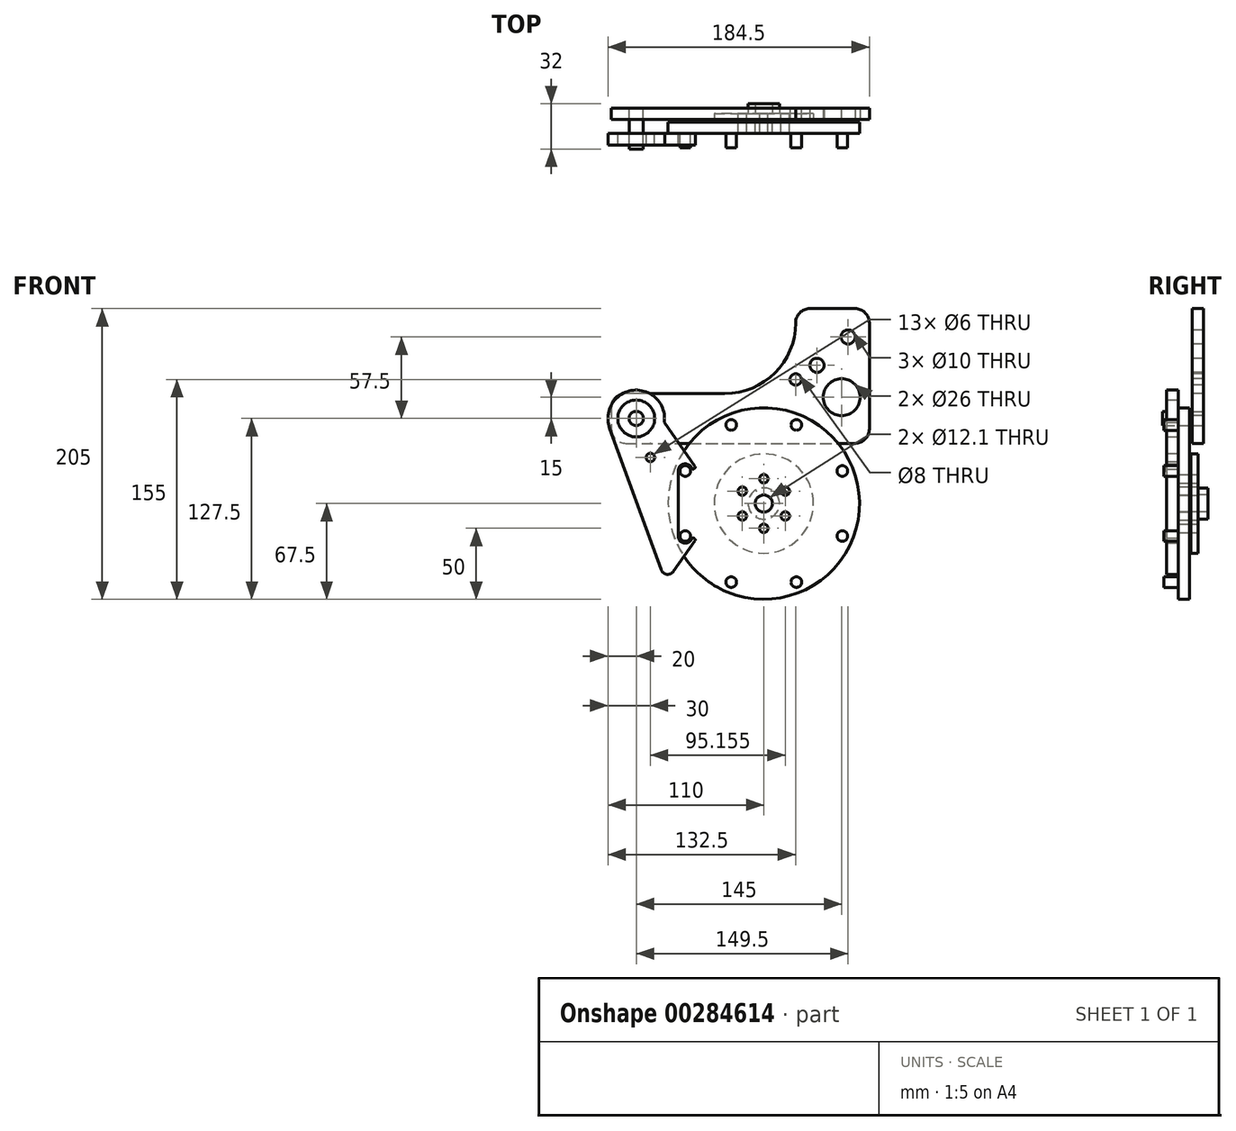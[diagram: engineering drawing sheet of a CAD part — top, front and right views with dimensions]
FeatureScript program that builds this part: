
annotation { "Feature Type Name" : "Feature", "Feature Type Description" : "" }
export const myFeature = defineFeature(function(context is Context, id is Id, definition is map)
    precondition{}
    {
        {
            var Q0;
            Q0=qCreatedBy(makeId("Front.planeOp"),FACE);
            var sketch = newSketch(context, id + "F0", { "sketchPlane" : qUnion([Q0])});
            skCircle(sketch, "E0", {"center": v(0, 0) * mm, "radius": 67.5 * mm});
            skCircle(sketch, "E1", {"center": v(0, 0) * mm, "radius": 6.05 * mm});
            skSolve(sketch);
        }
        {
            var Q0;
            Q0=qSketchRegion(id+"F0",true);
            extrude(context, id + "F1", {"entities" : qUnion([Q0]), "depth" : 5 * mm, "hasSecondDirection" : true, "secondDirectionOppositeDirection" : true, "secondDirectionDepth" : 3 * mm});
        }
        {
            var Q0;
            Q0=makeQuery(id+"F1.opExtrude","CAP_FACE",FACE,{"disambiguationData":[OSD([sQuery(id+"F0.wireOp",EDGE,"E0"),sQuery(id+"F0.wireOp",EDGE,"E1")])],"isStart":false});
            var sketch = newSketch(context, id + "F2", { "sketchPlane" : qUnion([Q0])});
            skCircle(sketch, "E2", {"center": v(0, 0) * mm, "radius": 60 * mm, "construction": true});
            skCircle(sketch, "E3", {"center": v(0, 60) * mm, "radius": 3.75 * mm});
            skCircle(sketch, "E4.1.0", {"center": v(-42.43, 42.43) * mm, "radius": 3.75 * mm});
            skCircle(sketch, "E4.2.0", {"center": v(-60, 0) * mm, "radius": 3.75 * mm});
            skCircle(sketch, "E4.3.0", {"center": v(-42.43, -42.43) * mm, "radius": 3.75 * mm});
            skCircle(sketch, "E4.4.0", {"center": v(0, -60) * mm, "radius": 3.75 * mm});
            skCircle(sketch, "E4.5.0", {"center": v(42.43, -42.43) * mm, "radius": 3.75 * mm});
            skCircle(sketch, "E4.6.0", {"center": v(60, 0) * mm, "radius": 3.75 * mm});
            skCircle(sketch, "E4.7.0", {"center": v(42.43, 42.43) * mm, "radius": 3.75 * mm});
            skPoint(sketch, "E5", {"position": v(0, -77) * mm});
            skSolve(sketch);
        }
        {
            var Q0;
            Q0=qSketchRegion(id+"F2",true);
            extrude(context, id + "F3", {"entities" : qUnion([Q0]), "operationType" : NewBodyOperationType.ADD, "depth" : 10 * mm});
        }
        {
            var Q0;
            Q0=qCreatedBy(makeId("Right.planeOp"),FACE);
            var sketch = newSketch(context, id + "F4", { "sketchPlane" : qUnion([Q0])});
            skLineSegment(sketch, "E6", {"start": v(-64.67, -77) * mm, "end": v(70.6, -77) * mm});
            skLineSegment(sketch, "E7", {"start": v(-72, 0) * mm, "end": v(117.3, 0) * mm});
            skLineSegment(sketch, "E8", {"start": v(-81.45, 67) * mm, "end": v(84.45, 67) * mm});
            skSolve(sketch);
        }
        {
            var Q0;
            Q0=makeQuery(id+"F1.opExtrude","CAP_FACE",FACE,{"disambiguationData":[OSD([sQuery(id+"F0.wireOp",EDGE,"E0"),sQuery(id+"F0.wireOp",EDGE,"E1")])],"isStart":false});
            var sketch = newSketch(context, id + "F5", { "sketchPlane" : qUnion([Q0])});
            skLineSegment(sketch, "E9", {"start": v(22.5, 127.5) * mm, "end": v(22.5, 127.5) * mm});
            skLineSegment(sketch, "E10", {"start": v(-27.5, 77.5) * mm, "end": v(-97.5, 77.5) * mm});
            skLineSegment(sketch, "E11", {"start": v(-107.5, 67.5) * mm, "end": v(-107.5, 52.5) * mm});
            skLineSegment(sketch, "E12", {"start": v(-97.5, 42.5) * mm, "end": v(-75.62, 42.5) * mm});
            skLineSegment(sketch, "E13", {"start": v(64.5, 137.5) * mm, "end": v(32.5, 137.5) * mm});
            skCircle(sketch, "E14", {"center": v(55, 75) * mm, "radius": 13 * mm});
            skCircle(sketch, "E15", {"center": v(-90, 60) * mm, "radius": 5 * mm});
            skCircle(sketch, "E16", {"center": v(59.5, 117.5) * mm, "radius": 5 * mm});
            skCircle(sketch, "E17", {"center": v(37.5, 97.5) * mm, "radius": 5 * mm});
            skPoint(sketch, "E18.visualSharp", {"position": v(-107.5, 77.5) * mm});
            skArc(sketch, "E18.filletArc", {"start": v(-97.5, 77.5) * mm, "mid": v(-104.57, 74.57) * mm, "end": v(-107.5, 67.5) * mm});
            skPoint(sketch, "E19.visualSharp", {"position": v(-107.5, 42.5) * mm});
            skArc(sketch, "E19.filletArc", {"start": v(-107.5, 52.5) * mm, "mid": v(-104.57, 45.43) * mm, "end": v(-97.5, 42.5) * mm});
            skArc(sketch, "E20.filletArc", {"start": v(-27.5, 77.5) * mm, "mid": v(7.86, 92.14) * mm, "end": v(22.5, 127.5) * mm});
            skArc(sketch, "E21.filletArc", {"start": v(32.5, 137.5) * mm, "mid": v(25.43, 134.57) * mm, "end": v(22.5, 127.5) * mm});
            skLineSegment(sketch, "E22", {"start": v(74.5, 127.5) * mm, "end": v(74.5, 52.5) * mm});
            skPoint(sketch, "E23.visualSharp", {"position": v(74.5, 137.5) * mm});
            skArc(sketch, "E23.filletArc", {"start": v(74.5, 127.5) * mm, "mid": v(71.57, 134.57) * mm, "end": v(64.5, 137.5) * mm});
            skPoint(sketch, "E24.visualSharp", {"position": v(74.5, 42.5) * mm});
            skArc(sketch, "E24.filletArc", {"start": v(64.5, 42.5) * mm, "mid": v(71.57, 45.43) * mm, "end": v(74.5, 52.5) * mm});
            skLineSegment(sketch, "E25.trimOffspring", {"start": v(-75.62, 42.5) * mm, "end": v(64.5, 42.5) * mm});
            skCircle(sketch, "E26", {"center": v(22.5, 87.5) * mm, "radius": 4 * mm});
            skSolve(sketch);
        }
        {
            var Q0;
            Q0=makeQuery(id+"F1.opExtrude","SWEPT_BODY",BODY,{"disambiguationData":[OSD([sQuery(id+"F0.wireOp",EDGE,"E0"),sQuery(id+"F0.wireOp",EDGE,"E1")])]});
            var Q1;
            Q1=sQuery(id+"F4.wireOp",EDGE,"E7");
            transform(context, id + "F6", {"entities" : qUnion([Q0]), "transformType" : TransformType.ROTATION, "transformAxis" : qUnion([Q1]), "angle" : 22.5 * degree, "makeCopy" : false});
        }
        {
            var Q0;
            Q0=qSketchRegion(id+"F5",true);
            extrude(context, id + "F7", {"entities" : qUnion([Q0]), "oppositeDirection" : true, "depth" : 8 * mm});
        }
        {
            var Q0;
            Q0=makeQuery(id+"F7.opExtrude","SWEPT_BODY",BODY,{"disambiguationData":[OSD([sQuery(id+"F5.wireOp",EDGE,"E9"),sQuery(id+"F5.wireOp",EDGE,"E10"),sQuery(id+"F5.wireOp",EDGE,"E11"),sQuery(id+"F5.wireOp",EDGE,"E12"),sQuery(id+"F5.wireOp",EDGE,"E13"),sQuery(id+"F5.wireOp",EDGE,"E14"),sQuery(id+"F5.wireOp",EDGE,"E15"),sQuery(id+"F5.wireOp",EDGE,"E16"),sQuery(id+"F5.wireOp",EDGE,"E17"),sQuery(id+"F5.wireOp",EDGE,"E18.filletArc"),sQuery(id+"F5.wireOp",EDGE,"E19.filletArc"),sQuery(id+"F5.wireOp",EDGE,"E20.filletArc"),sQuery(id+"F5.wireOp",EDGE,"E21.filletArc"),sQuery(id+"F5.wireOp",EDGE,"E22"),sQuery(id+"F5.wireOp",EDGE,"E23.filletArc"),sQuery(id+"F5.wireOp",EDGE,"E24.filletArc"),sQuery(id+"F5.wireOp",EDGE,"E25.trimOffspring")])]});
            transform(context, id + "F8", {"entities" : qUnion([Q0]), "transformType" : TransformType.TRANSLATION_3D, "dx" : 0 * mm, "dy" : 10 * mm, "dz" : 0 * mm, "makeCopy" : false});
        }
        {
            var Q0;
            Q0=makeQuery(id+"F1.opExtrude","CAP_FACE",FACE,{"disambiguationData":[OSD([sQuery(id+"F0.wireOp",EDGE,"E0"),sQuery(id+"F0.wireOp",EDGE,"E1")])],"isStart":false});
            var sketch = newSketch(context, id + "F9", { "sketchPlane" : qUnion([Q0])});
            skCircle(sketch, "E27", {"center": v(-90, 60) * mm, "radius": 13 * mm});
            skArc(sketch, "E28", {"start": v(-70.2, 57.14) * mm, "mid": v(-92.05, 79.9) * mm, "end": v(-108.8, 53.16) * mm});
            skLineSegment(sketch, "E29", {"start": v(-48.55, -26.21) * mm, "end": v(-63.67, -47.8) * mm});
            skLineSegment(sketch, "E30", {"start": v(-72.47, -46.65) * mm, "end": v(-108.8, 53.16) * mm});
            skPoint(sketch, "E31.visualSharp", {"position": v(-69.18, -55.67) * mm});
            skArc(sketch, "E31.filletArc", {"start": v(-72.47, -46.65) * mm, "mid": v(-68.42, -49.9) * mm, "end": v(-63.67, -47.8) * mm});
            skCircle(sketch, "E32", {"center": v(-80, 32.5) * mm, "radius": 3 * mm});
            skArc(sketch, "E33", {"start": v(-60.43, -22.96) * mm, "mid": v(-56.44, -27.86) * mm, "end": v(-50.84, -24.93) * mm});
            skLineSegment(sketch, "E34", {"start": v(-48.87, -24.77) * mm, "end": v(-49.42, -24.46) * mm});
            skPoint(sketch, "E35.visualSharp", {"position": v(-47.93, -25.32) * mm});
            skArc(sketch, "E35.filletArc", {"start": v(-48.55, -26.21) * mm, "mid": v(-48.4, -25.42) * mm, "end": v(-48.87, -24.77) * mm});
            skArc(sketch, "E36", {"start": v(-50.84, 24.93) * mm, "mid": v(-56.44, 27.86) * mm, "end": v(-60.43, 22.96) * mm});
            skLineSegment(sketch, "E37", {"start": v(-60.43, 22.96) * mm, "end": v(-60.43, -22.96) * mm});
            skLineSegment(sketch, "E38", {"start": v(-70.2, 57.14) * mm, "end": v(-48.55, 26.21) * mm});
            skLineSegment(sketch, "E39", {"start": v(-55.43, -22.96) * mm, "end": v(-50.5, -23.83) * mm, "construction": true});
            skPoint(sketch, "E40.visualSharp", {"position": v(-50.5, -23.83) * mm});
            skArc(sketch, "E40.filletArc", {"start": v(-49.42, -24.46) * mm, "mid": v(-50.23, -24.38) * mm, "end": v(-50.84, -24.93) * mm});
            skLineSegment(sketch, "E41", {"start": v(-55.43, 22.96) * mm, "end": v(-50.5, 23.83) * mm, "construction": true});
            skLineSegment(sketch, "E42", {"start": v(-48.87, 24.77) * mm, "end": v(-49.42, 24.46) * mm});
            skPoint(sketch, "E43.visualSharp", {"position": v(-50.5, 23.83) * mm});
            skArc(sketch, "E43.filletArc", {"start": v(-50.84, 24.93) * mm, "mid": v(-50.23, 24.38) * mm, "end": v(-49.42, 24.46) * mm});
            skPoint(sketch, "E44.visualSharp", {"position": v(-47.93, 25.32) * mm});
            skArc(sketch, "E44.filletArc", {"start": v(-48.87, 24.77) * mm, "mid": v(-48.4, 25.42) * mm, "end": v(-48.55, 26.21) * mm});
            skSolve(sketch);
        }
        {
            var Q0;
            Q0=qSketchRegion(id+"F9",true);
            extrude(context, id + "F10", {"entities" : qUnion([Q0]), "depth" : 8 * mm});
        }
        {
            var Q0;
            Q0=qCreatedBy(makeId("Top.planeOp"),FACE);
            var sketch = newSketch(context, id + "F11", { "sketchPlane" : qUnion([Q0])});
            skLineSegment(sketch, "E45", {"start": v(-6.05, 4) * mm, "end": v(-6.05, 16) * mm});
            skLineSegment(sketch, "E46", {"start": v(-6.05, 16) * mm, "end": v(-11.05, 16) * mm});
            skLineSegment(sketch, "E47", {"start": v(-11.05, 16) * mm, "end": v(-11.05, 9) * mm});
            skLineSegment(sketch, "E48", {"start": v(-11.05, 9) * mm, "end": v(-35, 9) * mm});
            skLineSegment(sketch, "E49", {"start": v(-35, 9) * mm, "end": v(-35, 4) * mm});
            skLineSegment(sketch, "E50", {"start": v(-35, 4) * mm, "end": v(-6.05, 4) * mm});
            skLineSegment(sketch, "E51", {"start": v(0, -36.2) * mm, "end": v(0, 47.53) * mm, "construction": true});
            skSolve(sketch);
        }
        {
            var Q0;
            Q0 = qSketchRegion(id + "F11", true);
            var Q1;
            Q1=sQuery(id+"F11.wireOp",EDGE,"E51");
            revolve(context, id + "F12", {"entities" : qUnion([Q0]), "axis" : qUnion([Q1]), "revolveType" : RevolveType.FULL});
        }
        {
            var Q0;
            Q0=makeQuery(id+"F12.opRevolve","SWEPT_FACE",FACE,{"disambiguationData":[OSD([sQuery(id+"F11.wireOp",EDGE,"E48")])]});
            var sketch = newSketch(context, id + "F13", { "sketchPlane" : qUnion([Q0])});
            skCircle(sketch, "E52", {"center": v(0, 17.5) * mm, "radius": 3 * mm});
            skCircle(sketch, "E53.1.0", {"center": v(-15.16, 8.75) * mm, "radius": 3 * mm});
            skCircle(sketch, "E53.2.0", {"center": v(-15.16, -8.75) * mm, "radius": 3 * mm});
            skCircle(sketch, "E53.3.0", {"center": v(0, -17.5) * mm, "radius": 3 * mm});
            skCircle(sketch, "E53.4.0", {"center": v(15.16, -8.75) * mm, "radius": 3 * mm});
            skPoint(sketch, "E53.center", {"position": v(0, 0) * mm});
            skCircle(sketch, "E54.1.5.0", {"center": v(15.16, 8.75) * mm, "radius": 3 * mm});
            skSolve(sketch);
        }
        {
            var Q0;
            Q0 = qSketchRegion(id + "F13", true);
            extrude(context, id + "F14", {"entities" : qUnion([Q0]), "operationType" : NewBodyOperationType.REMOVE, "oppositeDirection" : true, "depth" : 25 * mm});
        }
        {
            var Q0;
            Q0=makeQuery(id+"F7.opExtrude","CAP_FACE",FACE,{"disambiguationData":[OSD([sQuery(id+"F5.wireOp",EDGE,"E9"),sQuery(id+"F5.wireOp",EDGE,"E10"),sQuery(id+"F5.wireOp",EDGE,"E11"),sQuery(id+"F5.wireOp",EDGE,"E12"),sQuery(id+"F5.wireOp",EDGE,"E13"),sQuery(id+"F5.wireOp",EDGE,"E14"),sQuery(id+"F5.wireOp",EDGE,"E15"),sQuery(id+"F5.wireOp",EDGE,"E16"),sQuery(id+"F5.wireOp",EDGE,"E17"),sQuery(id+"F5.wireOp",EDGE,"E18.filletArc"),sQuery(id+"F5.wireOp",EDGE,"E19.filletArc"),sQuery(id+"F5.wireOp",EDGE,"E20.filletArc"),sQuery(id+"F5.wireOp",EDGE,"E21.filletArc"),sQuery(id+"F5.wireOp",EDGE,"E22"),sQuery(id+"F5.wireOp",EDGE,"E23.filletArc"),sQuery(id+"F5.wireOp",EDGE,"E24.filletArc"),sQuery(id+"F5.wireOp",EDGE,"E25.trimOffspring")])],"isStart":false});
            var sketch = newSketch(context, id + "F15", { "sketchPlane" : qUnion([Q0])});
            skCircle(sketch, "E55", {"center": v(90, 60) * mm, "radius": 5 * mm});
            skSolve(sketch);
        }
        {
            var Q0;
            Q0 = qSketchRegion(id + "F15", true);
            extrude(context, id + "F16", {"entities" : qUnion([Q0]), "oppositeDirection" : true, "depth" : 29 * mm});
        }
    });
